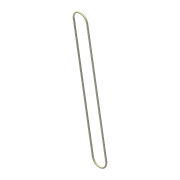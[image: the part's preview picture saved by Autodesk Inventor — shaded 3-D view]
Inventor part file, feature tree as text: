
AUTODESK INVENTOR PART (.ipt)
format: ipt  version: 2012 (Build 160160000, 160)  size: 96,256 bytes
history: native  units: in
note: dims shown in document units (in); Inventor stores cm internally (conversion verified against a paired STEP export)
features: extrude x1, fillet x1, sketch x1
ambient origin geometry x8: Origin, YZ Plane, XZ Plane, XY Plane, X Axis, Y Axis, Z Axis, Center Point
bodies: Solid1 (feature_tree)
feature tree (3):
  extrude  "Extrusion1"  Depth=1.0in
  fillet  "Fillet2"  Radius=0.1875in
  sketch  "Sketch1"  dims[d0=1.0in d1=1.0in d2=0.1875in d3=0.1875in d4=0.1875in d5=0.0in d7=0.0938in]
